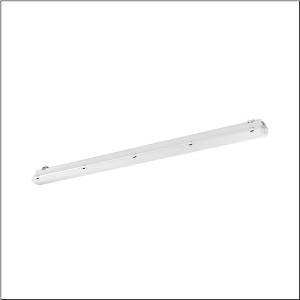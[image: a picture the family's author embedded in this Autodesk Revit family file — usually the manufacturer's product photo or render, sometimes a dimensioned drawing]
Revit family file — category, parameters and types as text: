
# Revit family: monsun_r__11xtreme_mo_51fe10dp460j_08a3
name_source: partatom
category: Lighting Fixtures
units: mm (PartAtom-declared; Revit-internal decimal feet)

## family parameters
Cut with Voids When Loaded = No
Host = Face
Light Source = No
Part Type = Normal
Room Calculation Point = No
Round Connector Dimension = Use Diameter
Shared = No

## types (1)
- --- (1 x LED, 6370 lm, 36.5 W, 4000K)
    Apparent Load = 37 VA
    CIE Flux Codes = 47 77 93 94 100
    Color Rendering = 80
    Color Temperature = 4000K
    Default Elevation = 1800 mm
    Description = Monsun® 11Xtreme MO, damp-proof luminaire, chain hanger, primary optical cover: enclosure, of PMMA, light emission: direct distribution, primary light characteristic: symmetric, installation type: suspended mounting, surface-mounted, horizontal mounting, vertical mounting, LED, rated luminous flux: 6.370lm, luminous efficacy: 175lm/W, light colour: 840, colour temperature: 4000K, control gear: ECG DALI, with terminal, 5-pole, max. 2.5mm², mains connection: 220..240V, AC, 50/60Hz, rated input power: 37W, luminaire housing, of glass-fibre reinforced polyester, uncoated, bright grey, incl. chain hanger, length: 1.590mm, width: 90mm, height: 88mm, clip for enclosure, of stainless steel (V2A), ceiling mounting element, of stainless steel (V2A), chain hanger, of stainless steel (V2A), protection rating (complete): IP66, insulation class (complete): insulation class I (protective earthing), certification: CE, ENEC, VDE, UKCA, protection symbol: D, impact resistance: IK04, permissible operating ambient temperature: -35..+55°C, standard: EN 60598-2-1, EN 50419, corresponds to IFS (International Featured Standards) requirements for safety and quality in the food industry, for indoor or canopied outdoor use, no direct snow, no direct sun, no direct rain, contact your sales advisor before using the luminaires in applications with unclear chemical exposure, large temperature fluctuations or condensation-forming humidity, LABS conformity tested according to VDMA 24364:2018-05, packaging unit: 1 piece
    Height = 88 mm
    Lamp = 1 x LED
    Lamp Light Flux = 6370 lm
    Lamp Power = 36.5 W
    Lamp count = 1
    Length = 1590 mm
    Luminous efficacy = 175 lm/W
    Manufacturer = Siteco
    ModVariant = No
    Model = 51FE10DP460J
    Mounting Place = Ceiling
    Mounting Type = Surface mounted
    Number of Poles = 1
    OnlyDefault = Yes
    Power Factor = 1
    Product Name = Monsun® 11Xtreme MO
    Product group = damp-proof luminaire
    ProductGroupID = 301
    Protection Class = Protection class I
    Protection Degree = IP 66
    RLX_Detail_Level = 1
    RLX_Emergency_Light_Flux = 0 lm
    RLX_Emergency_Type = 0
    RLX_Emergency_Type_DB = No
    RlxData = <blob elided: 88053 chars, md5=08a36630>
    Socket = socket
    Standby Power = 0 W
    System Light Flux = 6370 lm
    System Power = 37 W
    Type Comments = factory setting: luminous flux: 100 % | dim-lin: 254 | 240 mA
    Type Image = l_1006851.jpg
    URL = http://relux.com
    VarID = @adj_151167
    Voltage = 0 V
    Weight = 0.00 kg
    Width = 90 mm

## geometry (parser evidence)
native form markers: Blend x4, Sweep x12
no freeform markers — native parametric forms only
